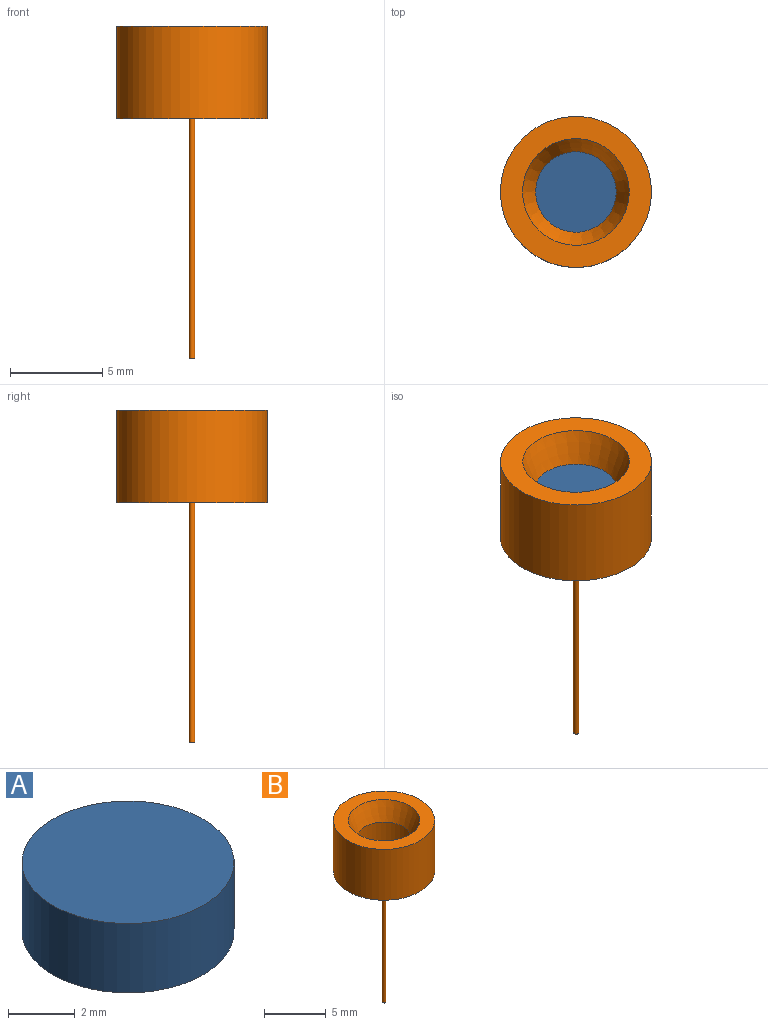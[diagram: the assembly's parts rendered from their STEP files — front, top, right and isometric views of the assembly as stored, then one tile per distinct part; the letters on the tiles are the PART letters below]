
ASSEMBLY  parts=2 mates=1
PART A: 3 faces, bbox 6.4x6.4x2.5 mm
  f0: cylinder r=3.17mm len=6.35mm, axis (0,0,-1), area 50.7mm2, adj f1,f2
  f1: plane 6.35x6.35mm, normal (0,0,1), area 31.7mm2, adj f0
  f2: plane 6.35x6.35mm, normal (0,0,-1), area 31.7mm2, adj f0
PART B: 9 faces, bbox 8.2x8.2x18 mm
  f0: plane 6.35x6.35mm, normal (0,0,1), area 31.7mm2, adj f1
  f1: cylinder r=3.17mm len=6.35mm, axis (0,0,1), area 50.7mm2, adj f0,f2
  f2: plane 6.35x6.35mm, normal (0,0,-1), area 16.8mm2, adj f1,f3
  f3: cone r=2.89mm half-angle=22.3deg, axis (0,0,1), area 29.7mm2, adj f2,f4
  f4: plane 8.18x8.18mm, normal (0,0,1), area 26.4mm2, adj f3,f5
  f5: cylinder r=4.09mm len=8.18mm, axis (0,0,1), area 129.2mm2, adj f4,f6
  f6: plane 8.18x8.18mm, normal (0,0,-1), area 52.5mm2, adj f5,f7
  f7: cylinder r=0.15mm len=12.95mm, axis (0,0,1), area 12.4mm2, adj f6,f8
  f8: plane 0.3x0.3mm, normal (0,0,-1), area 0.1mm2, adj f7
PLACE A t=(-2.63,-3.18,0.84)mm
PLACE B t=(-2.63,-3.18,-1.19)mm fixed
MATE fastened A.f0 <-> B.f1  axis (0,0,-1) through (-2.63,-3.18,-0.43)mm
